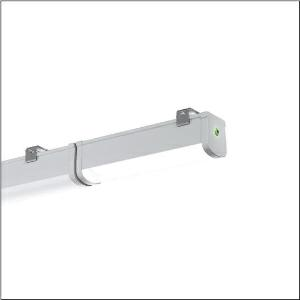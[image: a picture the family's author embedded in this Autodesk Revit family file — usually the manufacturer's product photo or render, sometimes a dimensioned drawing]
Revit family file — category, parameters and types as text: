
# Revit family: monsun_r__31_58fa207a403b3g_c1e4
name_source: partatom
category: Lighting Fixtures
units: mm (PartAtom-declared; Revit-internal decimal feet)

## family parameters
Cut with Voids When Loaded = No
Host = Face
Light Source = No
Part Type = Normal
Room Calculation Point = No
Round Connector Dimension = Use Diameter
Shared = No

## types (1)
- --- (1 x LED, 450 lm, 5 W, 4000K)
    Apparent Load = 5 VA
    CIE Flux Codes = 42 72 91 92 100
    Color Rendering = 80
    Color Temperature = 4000K
    Default Elevation = 1800 mm
    Description = Monsun® 31, emergency light element, primary optical cover: diffuser, of PC, frosted, light emission: direct distribution, primary light characteristic: symmetric, installation type: surface-mounted, EM-KIT 3h,LED, rated luminous flux: 450lm, luminous efficacy: 100lm/W, light colour: 840, colour temperature: 4000K, control gear: without control gear, emergency light function, with socket/plug, mains connection: 220..240V, AC, 50..60Hz, rated input power: 5W, housing, luminaire housing, of PC, light grey (RAL 7035), length: 297mm, width: 68mm, height: 76mm, protection rating (complete): IP65, insulation class (complete): insulation class II (safety insulation), certification: CE, protection symbol: D, impact resistance: IK08, permissible operating ambient temperature: 0..+40°C, standard: EN 60598-2-22, corresponds to IFS (International Featured Standards) requirements for safety and quality in the food industry, packaging unit: 1 piece
    Height = 77 mm
    Lamp = 1 x LED
    Lamp Light Flux = 450 lm
    Lamp Power = 5 W
    Lamp count = 1
    Length = 294 mm
    Luminous efficacy = 90 lm/W
    Manufacturer = Siteco
    ModVariant = No
    Model = 58FA207A403B3G
    Mounting Place = Ceiling
    Mounting Type = Surface mounted
    Number of Poles = 1
    OnlyDefault = Yes
    Power Factor = 1
    Product Name = Monsun® 31
    Product group = emergency light element
    ProductGroupID = 307
    Protection Class = Protection class II
    Protection Degree = IP 65
    RLX_Detail_Level = 1
    RLX_Emergency_Light_Flux = 0 lm
    RLX_Emergency_Type = 0
    RLX_Emergency_Type_DB = No
    RlxData = <blob elided: 31201 chars, md5=84352f34>
    Socket = socket
    Standby Power = 0 W
    System Light Flux = 450 lm
    System Power = 5 W
    Type Comments = : 3 h
    Type Image = l_1006658.jpg
    URL = http://relux.com
    VarID = @adj_171881
    Voltage = 0 V
    Weight = 0.00 kg
    Width = 69 mm

## geometry (parser evidence)
native form markers: Blend x4, Sweep x12
no freeform markers — native parametric forms only
